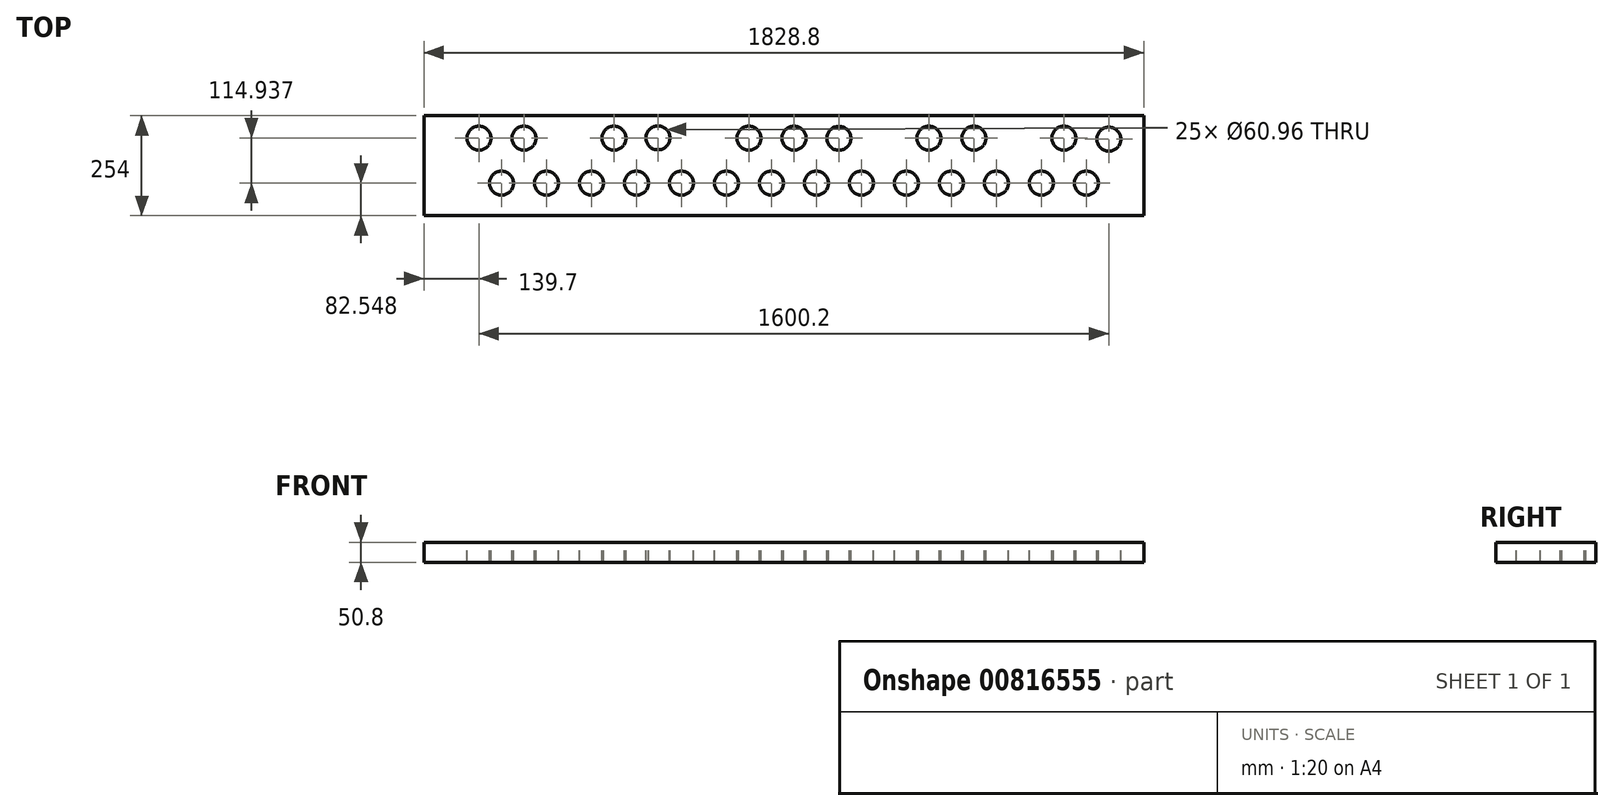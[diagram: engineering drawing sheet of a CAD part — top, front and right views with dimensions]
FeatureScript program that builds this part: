
annotation { "Feature Type Name" : "Feature", "Feature Type Description" : "" }
export const myFeature = defineFeature(function(context is Context, id is Id, definition is map)
    precondition{}
    {
        {
            var Q0;
            Q0=qCreatedBy(makeId("Right.planeOp"),FACE);
            var sketch = newSketch(context, id + "F0", { "sketchPlane" : qUnion([Q0])});
            skLineSegment(sketch, "E0.bottom", {"start": v(-137.62, -67.7) * mm, "end": v(116.38, -67.7) * mm});
            skLineSegment(sketch, "E0.top", {"start": v(-137.62, -118.5) * mm, "end": v(116.38, -118.5) * mm});
            skLineSegment(sketch, "E0.left", {"start": v(-137.62, -67.7) * mm, "end": v(-137.62, -118.5) * mm});
            skLineSegment(sketch, "E0.right", {"start": v(116.38, -67.7) * mm, "end": v(116.38, -118.5) * mm});
            skSolve(sketch);
        }
        {
            var Q0;
            Q0=makeQuery(id+"F0.imprint","IMPRINT",FACE,{"disambiguationData":[TD([[makeQuery(id+"F0.imprint","IMPRINT",EDGE,{"derivedFrom":sQuery(id+"F0.wireOp",EDGE,"E0.bottom")}),-1.0]])]});
            extrude(context, id + "F1", {"entities" : qUnion([Q0]), "depth" : 1828.8 * mm, "offsetDistance" : 25.4 * mm});
        }
        {
            var Q0;
            Q0=qCreatedBy(makeId("Top.planeOp"),FACE);
            var sketch = newSketch(context, id + "F2", { "sketchPlane" : qUnion([Q0])});
            skCircle(sketch, "E1", {"center": v(139.7, 59.23) * mm, "radius": 30.48 * mm});
            skCircle(sketch, "E2", {"center": v(254, 59.23) * mm, "radius": 30.48 * mm});
            skCircle(sketch, "E3", {"center": v(196.9, -55.07) * mm, "radius": 30.48 * mm});
            skCircle(sketch, "E4", {"center": v(311.2, -55.07) * mm, "radius": 30.48 * mm});
            skCircle(sketch, "E5", {"center": v(425.5, -55.07) * mm, "radius": 30.48 * mm});
            skCircle(sketch, "E6", {"center": v(539.8, -55.07) * mm, "radius": 30.48 * mm});
            skCircle(sketch, "E7", {"center": v(654.1, -55.07) * mm, "radius": 30.48 * mm});
            skCircle(sketch, "E8", {"center": v(768.4, -55.07) * mm, "radius": 30.48 * mm});
            skCircle(sketch, "E9", {"center": v(882.7, -55.07) * mm, "radius": 30.48 * mm});
            skCircle(sketch, "E10", {"center": v(997, -55.07) * mm, "radius": 30.48 * mm});
            skCircle(sketch, "E11", {"center": v(1111.3, -55.07) * mm, "radius": 30.48 * mm});
            skCircle(sketch, "E12", {"center": v(1225.6, -55.07) * mm, "radius": 30.48 * mm});
            skCircle(sketch, "E13", {"center": v(1339.9, -55.07) * mm, "radius": 30.48 * mm});
            skCircle(sketch, "E14", {"center": v(1454.2, -55.07) * mm, "radius": 30.48 * mm});
            skCircle(sketch, "E15", {"center": v(1568.5, -55.07) * mm, "radius": 30.48 * mm});
            skCircle(sketch, "E16", {"center": v(1682.8, -55.07) * mm, "radius": 30.48 * mm});
            skCircle(sketch, "E17", {"center": v(482.6, 59.23) * mm, "radius": 30.48 * mm});
            skCircle(sketch, "E18", {"center": v(594.4, 59.87) * mm, "radius": 30.48 * mm});
            skCircle(sketch, "E19", {"center": v(825.5, 59.23) * mm, "radius": 30.48 * mm});
            skCircle(sketch, "E20", {"center": v(940.11, 59.23) * mm, "radius": 30.48 * mm});
            skCircle(sketch, "E21", {"center": v(1054.1, 58.8) * mm, "radius": 30.48 * mm});
            skCircle(sketch, "E22", {"center": v(1282.7, 59.23) * mm, "radius": 30.48 * mm});
            skCircle(sketch, "E23", {"center": v(1397, 59.23) * mm, "radius": 30.48 * mm});
            skCircle(sketch, "E24", {"center": v(1625.6, 59.23) * mm, "radius": 30.48 * mm});
            skCircle(sketch, "E25", {"center": v(1739.9, 56.67) * mm, "radius": 30.48 * mm});
            skSolve(sketch);
        }
        {
            var Q0;
            Q0=makeQuery(id+"F2.imprint","IMPRINT",FACE,{"disambiguationData":[TD([[makeQuery(id+"F2.imprint","IMPRINT",EDGE,{"derivedFrom":sQuery(id+"F2.wireOp",EDGE,"E1")}),1.0]])]});
            var Q1;
            Q1=makeQuery(id+"F2.imprint","IMPRINT",FACE,{"disambiguationData":[TD([[makeQuery(id+"F2.imprint","IMPRINT",EDGE,{"derivedFrom":sQuery(id+"F2.wireOp",EDGE,"E2")}),1.0]])]});
            var Q2;
            Q2=makeQuery(id+"F2.imprint","IMPRINT",FACE,{"disambiguationData":[TD([[makeQuery(id+"F2.imprint","IMPRINT",EDGE,{"derivedFrom":sQuery(id+"F2.wireOp",EDGE,"E3")}),1.0]])]});
            var Q3;
            Q3=makeQuery(id+"F2.imprint","IMPRINT",FACE,{"disambiguationData":[TD([[makeQuery(id+"F2.imprint","IMPRINT",EDGE,{"derivedFrom":sQuery(id+"F2.wireOp",EDGE,"E4")}),1.0]])]});
            var Q4;
            Q4=makeQuery(id+"F2.imprint","IMPRINT",FACE,{"disambiguationData":[TD([[makeQuery(id+"F2.imprint","IMPRINT",EDGE,{"derivedFrom":sQuery(id+"F2.wireOp",EDGE,"E5")}),1.0]])]});
            var Q5;
            Q5=makeQuery(id+"F2.imprint","IMPRINT",FACE,{"disambiguationData":[TD([[makeQuery(id+"F2.imprint","IMPRINT",EDGE,{"derivedFrom":sQuery(id+"F2.wireOp",EDGE,"E6")}),1.0]])]});
            var Q6;
            Q6=makeQuery(id+"F2.imprint","IMPRINT",FACE,{"disambiguationData":[TD([[makeQuery(id+"F2.imprint","IMPRINT",EDGE,{"derivedFrom":sQuery(id+"F2.wireOp",EDGE,"E17")}),1.0]])]});
            var Q7;
            Q7=makeQuery(id+"F2.imprint","IMPRINT",FACE,{"disambiguationData":[TD([[makeQuery(id+"F2.imprint","IMPRINT",EDGE,{"derivedFrom":sQuery(id+"F2.wireOp",EDGE,"E18")}),1.0]])]});
            var Q8;
            Q8=makeQuery(id+"F2.imprint","IMPRINT",FACE,{"disambiguationData":[TD([[makeQuery(id+"F2.imprint","IMPRINT",EDGE,{"derivedFrom":sQuery(id+"F2.wireOp",EDGE,"E7")}),1.0]])]});
            var Q9;
            Q9=makeQuery(id+"F2.imprint","IMPRINT",FACE,{"disambiguationData":[TD([[makeQuery(id+"F2.imprint","IMPRINT",EDGE,{"derivedFrom":sQuery(id+"F2.wireOp",EDGE,"E8")}),1.0]])]});
            var Q10;
            Q10=makeQuery(id+"F2.imprint","IMPRINT",FACE,{"disambiguationData":[TD([[makeQuery(id+"F2.imprint","IMPRINT",EDGE,{"derivedFrom":sQuery(id+"F2.wireOp",EDGE,"E9")}),1.0]])]});
            var Q11;
            Q11=makeQuery(id+"F2.imprint","IMPRINT",FACE,{"disambiguationData":[TD([[makeQuery(id+"F2.imprint","IMPRINT",EDGE,{"derivedFrom":sQuery(id+"F2.wireOp",EDGE,"E19")}),1.0]])]});
            var Q12;
            Q12=makeQuery(id+"F2.imprint","IMPRINT",FACE,{"disambiguationData":[TD([[makeQuery(id+"F2.imprint","IMPRINT",EDGE,{"derivedFrom":sQuery(id+"F2.wireOp",EDGE,"E20")}),1.0]])]});
            var Q13;
            Q13=makeQuery(id+"F2.imprint","IMPRINT",FACE,{"disambiguationData":[TD([[makeQuery(id+"F2.imprint","IMPRINT",EDGE,{"derivedFrom":sQuery(id+"F2.wireOp",EDGE,"E10")}),1.0]])]});
            var Q14;
            Q14=makeQuery(id+"F2.imprint","IMPRINT",FACE,{"disambiguationData":[TD([[makeQuery(id+"F2.imprint","IMPRINT",EDGE,{"derivedFrom":sQuery(id+"F2.wireOp",EDGE,"E11")}),1.0]])]});
            var Q15;
            Q15=makeQuery(id+"F2.imprint","IMPRINT",FACE,{"disambiguationData":[TD([[makeQuery(id+"F2.imprint","IMPRINT",EDGE,{"derivedFrom":sQuery(id+"F2.wireOp",EDGE,"E21")}),1.0]])]});
            var Q16;
            Q16=makeQuery(id+"F2.imprint","IMPRINT",FACE,{"disambiguationData":[TD([[makeQuery(id+"F2.imprint","IMPRINT",EDGE,{"derivedFrom":sQuery(id+"F2.wireOp",EDGE,"E12")}),1.0]])]});
            var Q17;
            Q17=makeQuery(id+"F2.imprint","IMPRINT",FACE,{"disambiguationData":[TD([[makeQuery(id+"F2.imprint","IMPRINT",EDGE,{"derivedFrom":sQuery(id+"F2.wireOp",EDGE,"E13")}),1.0]])]});
            var Q18;
            Q18=makeQuery(id+"F2.imprint","IMPRINT",FACE,{"disambiguationData":[TD([[makeQuery(id+"F2.imprint","IMPRINT",EDGE,{"derivedFrom":sQuery(id+"F2.wireOp",EDGE,"E22")}),1.0]])]});
            var Q19;
            Q19=makeQuery(id+"F2.imprint","IMPRINT",FACE,{"disambiguationData":[TD([[makeQuery(id+"F2.imprint","IMPRINT",EDGE,{"derivedFrom":sQuery(id+"F2.wireOp",EDGE,"E23")}),1.0]])]});
            var Q20;
            Q20=makeQuery(id+"F2.imprint","IMPRINT",FACE,{"disambiguationData":[TD([[makeQuery(id+"F2.imprint","IMPRINT",EDGE,{"derivedFrom":sQuery(id+"F2.wireOp",EDGE,"E14")}),1.0]])]});
            var Q21;
            Q21=makeQuery(id+"F2.imprint","IMPRINT",FACE,{"disambiguationData":[TD([[makeQuery(id+"F2.imprint","IMPRINT",EDGE,{"derivedFrom":sQuery(id+"F2.wireOp",EDGE,"E15")}),1.0]])]});
            var Q22;
            Q22=makeQuery(id+"F2.imprint","IMPRINT",FACE,{"disambiguationData":[TD([[makeQuery(id+"F2.imprint","IMPRINT",EDGE,{"derivedFrom":sQuery(id+"F2.wireOp",EDGE,"E24")}),1.0]])]});
            var Q23;
            Q23=makeQuery(id+"F2.imprint","IMPRINT",FACE,{"disambiguationData":[TD([[makeQuery(id+"F2.imprint","IMPRINT",EDGE,{"derivedFrom":sQuery(id+"F2.wireOp",EDGE,"E16")}),1.0]])]});
            var Q24;
            Q24=makeQuery(id+"F2.imprint","IMPRINT",FACE,{"disambiguationData":[TD([[makeQuery(id+"F2.imprint","IMPRINT",EDGE,{"derivedFrom":sQuery(id+"F2.wireOp",EDGE,"0f8d663a-2af9-4bdc-ba64-bc605e7f9e2e")}),1.0]])]});
            var Q25;
            Q25=makeQuery(id+"F2.imprint","IMPRINT",FACE,{"disambiguationData":[TD([[makeQuery(id+"F2.imprint","IMPRINT",EDGE,{"derivedFrom":sQuery(id+"F2.wireOp",EDGE,"E25")}),1.0]])]});
            extrude(context, id + "F3", {"entities" : qUnion([Q0, Q1, Q2, Q3, Q4, Q5, Q6, Q7, Q8, Q9, Q10, Q11, Q12, Q13, Q14, Q15, Q16, Q17, Q18, Q19, Q20, Q21, Q22, Q23, Q24, Q25]), "operationType" : NewBodyOperationType.REMOVE, "oppositeDirection" : true, "depth" : 127 * mm});
        }
    });
